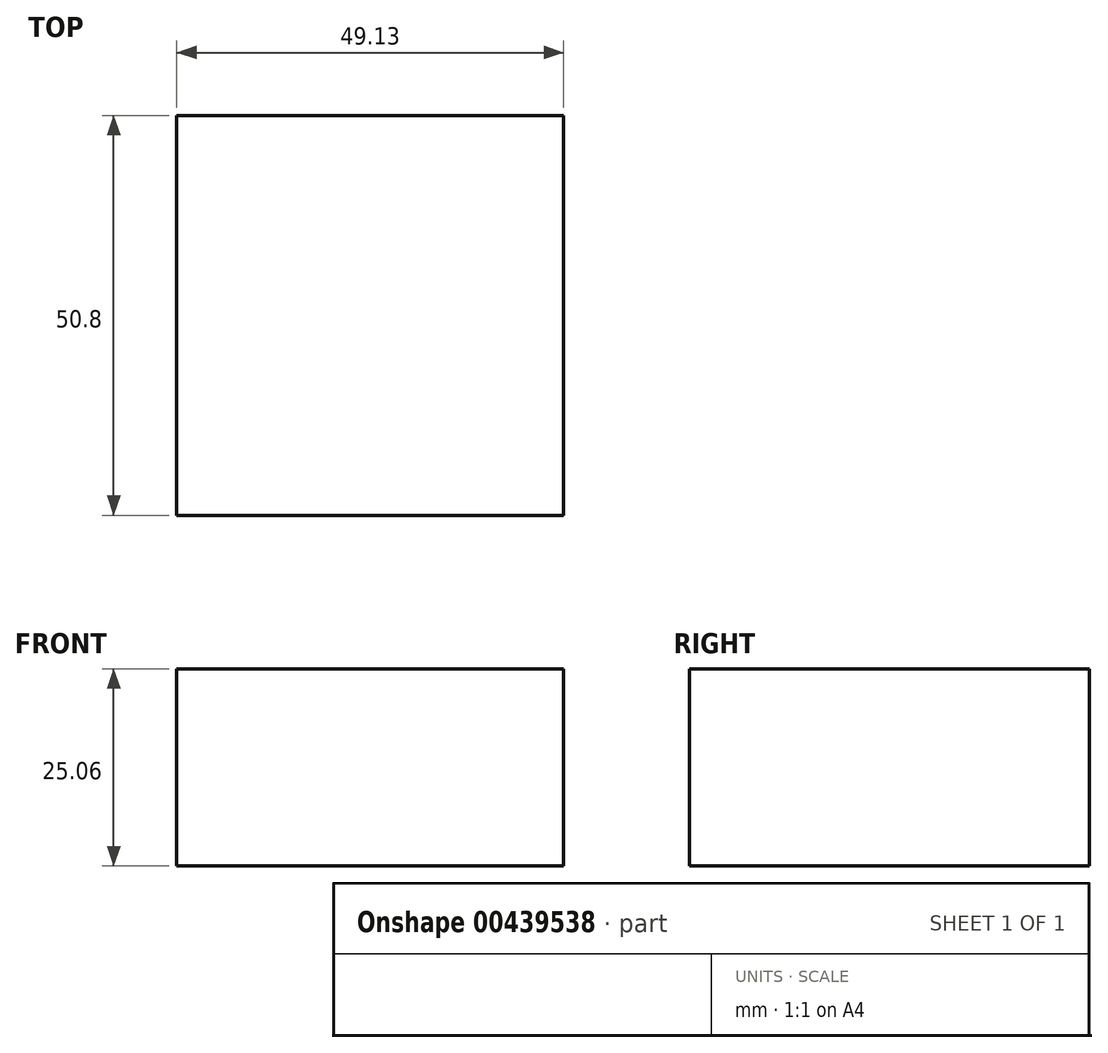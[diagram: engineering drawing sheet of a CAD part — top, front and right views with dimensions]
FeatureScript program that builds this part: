
annotation { "Feature Type Name" : "Feature", "Feature Type Description" : "" }
export const myFeature = defineFeature(function(context is Context, id is Id, definition is map)
    precondition{}
    {
        {
            var Q0;
            Q0=qCreatedBy(makeId("Front.planeOp"),FACE);
            var sketch = newSketch(context, id + "F0", { "sketchPlane" : qUnion([Q0])});
            skLineSegment(sketch, "E0.bottom", {"start": v(0, 0) * mm, "end": v(49.13, 0) * mm});
            skLineSegment(sketch, "E0.top", {"start": v(0, -25.06) * mm, "end": v(49.13, -25.06) * mm});
            skLineSegment(sketch, "E0.left", {"start": v(0, 0) * mm, "end": v(0, -25.06) * mm});
            skLineSegment(sketch, "E0.right", {"start": v(49.13, 0) * mm, "end": v(49.13, -25.06) * mm});
            skSolve(sketch);
        }
        {
            var Q0;
            Q0=makeQuery(id+"F0.imprint","IMPRINT",FACE,{"disambiguationData":[TD([[makeQuery(id+"F0.imprint","IMPRINT",EDGE,{"derivedFrom":sQuery(id+"F0.wireOp",EDGE,"E0.bottom")}),-1.0]])]});
            extrude(context, id + "F1", {"entities" : qUnion([Q0]), "depth" : 50.8 * mm});
        }
    });
